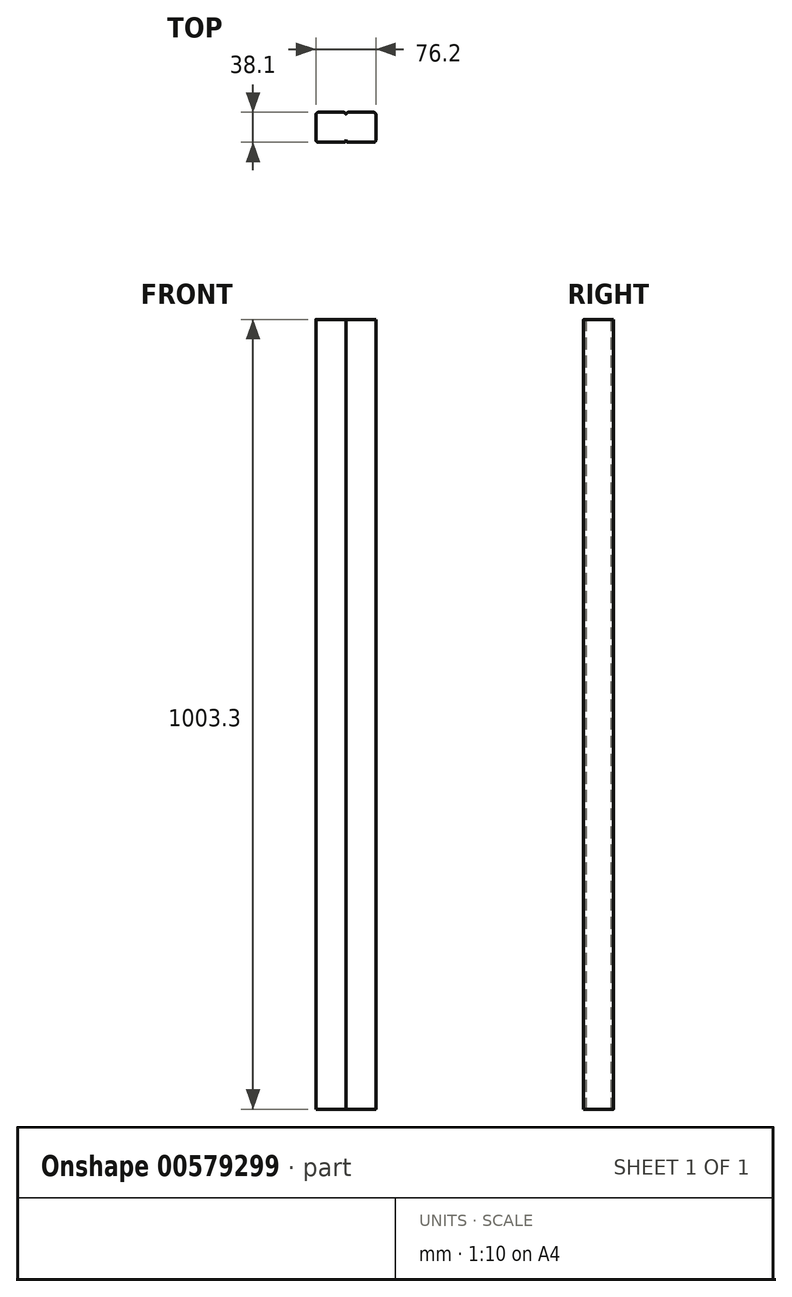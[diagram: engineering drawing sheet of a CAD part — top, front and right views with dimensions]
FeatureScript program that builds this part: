
annotation { "Feature Type Name" : "Feature", "Feature Type Description" : "" }
export const myFeature = defineFeature(function(context is Context, id is Id, definition is map)
    precondition{}
    {
        {
            var Q0;
            Q0=qCreatedBy(makeId("Top.planeOp"),FACE);
            var sketch = newSketch(context, id + "F0", { "sketchPlane" : qUnion([Q0])});
            skLineSegment(sketch, "E0.bottom", {"start": v(34.93, 19.05) * mm, "end": v(3.18, 19.05) * mm});
            skLineSegment(sketch, "E0.top", {"start": v(34.93, -19.05) * mm, "end": v(3.18, -19.05) * mm});
            skLineSegment(sketch, "E0.left", {"start": v(38.1, 15.88) * mm, "end": v(38.1, -15.87) * mm});
            skLineSegment(sketch, "E0.right", {"start": v(-38.1, 15.88) * mm, "end": v(-38.1, -15.88) * mm});
            skPoint(sketch, "E0.middle", {"position": v(0, 0) * mm});
            skLineSegment(sketch, "E1", {"start": v(0, 15.88) * mm, "end": v(0, -15.88) * mm});
            skPoint(sketch, "E2.newPointA", {"position": v(0, 19.05) * mm});
            skPoint(sketch, "E2.newPointB", {"position": v(-38.1, 19.05) * mm});
            skArc(sketch, "E2.filletArc", {"start": v(3.18, 19.05) * mm, "mid": v(0.93, 18.12) * mm, "end": v(0, 15.88) * mm});
            skPoint(sketch, "E3.visualSharp", {"position": v(38.1, 19.05) * mm});
            skArc(sketch, "E3.filletArc", {"start": v(38.1, 15.88) * mm, "mid": v(37.17, 18.12) * mm, "end": v(34.93, 19.05) * mm});
            skPoint(sketch, "E4.visualSharp", {"position": v(38.1, -19.05) * mm});
            skArc(sketch, "E4.filletArc", {"start": v(34.93, -19.05) * mm, "mid": v(37.17, -18.12) * mm, "end": v(38.1, -15.87) * mm});
            skPoint(sketch, "E5.newPointA", {"position": v(-38.1, -19.05) * mm});
            skPoint(sketch, "E5.newPointB", {"position": v(0, -19.05) * mm});
            skArc(sketch, "E5.filletArc", {"start": v(0, -15.88) * mm, "mid": v(0.93, -18.12) * mm, "end": v(3.17, -19.05) * mm});
            skLineSegment(sketch, "E6.bottom", {"start": v(-34.93, 19.05) * mm, "end": v(-3.18, 19.05) * mm});
            skLineSegment(sketch, "E6.top", {"start": v(-34.93, -19.05) * mm, "end": v(-3.18, -19.05) * mm});
            skArc(sketch, "E7.filletArc", {"start": v(-34.93, 19.05) * mm, "mid": v(-37.17, 18.12) * mm, "end": v(-38.1, 15.88) * mm});
            skArc(sketch, "E8.filletArc", {"start": v(0, 15.88) * mm, "mid": v(-0.93, 18.12) * mm, "end": v(-3.18, 19.05) * mm});
            skArc(sketch, "E9.filletArc", {"start": v(-3.18, -19.05) * mm, "mid": v(-0.93, -18.12) * mm, "end": v(0, -15.88) * mm});
            skArc(sketch, "E10.filletArc", {"start": v(-38.1, -15.88) * mm, "mid": v(-37.17, -18.12) * mm, "end": v(-34.93, -19.05) * mm});
            skSolve(sketch);
        }
        {
            var Q0;
            Q0=qSketchRegion(id+"F0",true);
            extrude(context, id + "F1", {"entities" : qUnion([Q0]), "depth" : 1003.3 * mm, "offsetDistance" : 25.4 * mm});
        }
    });
